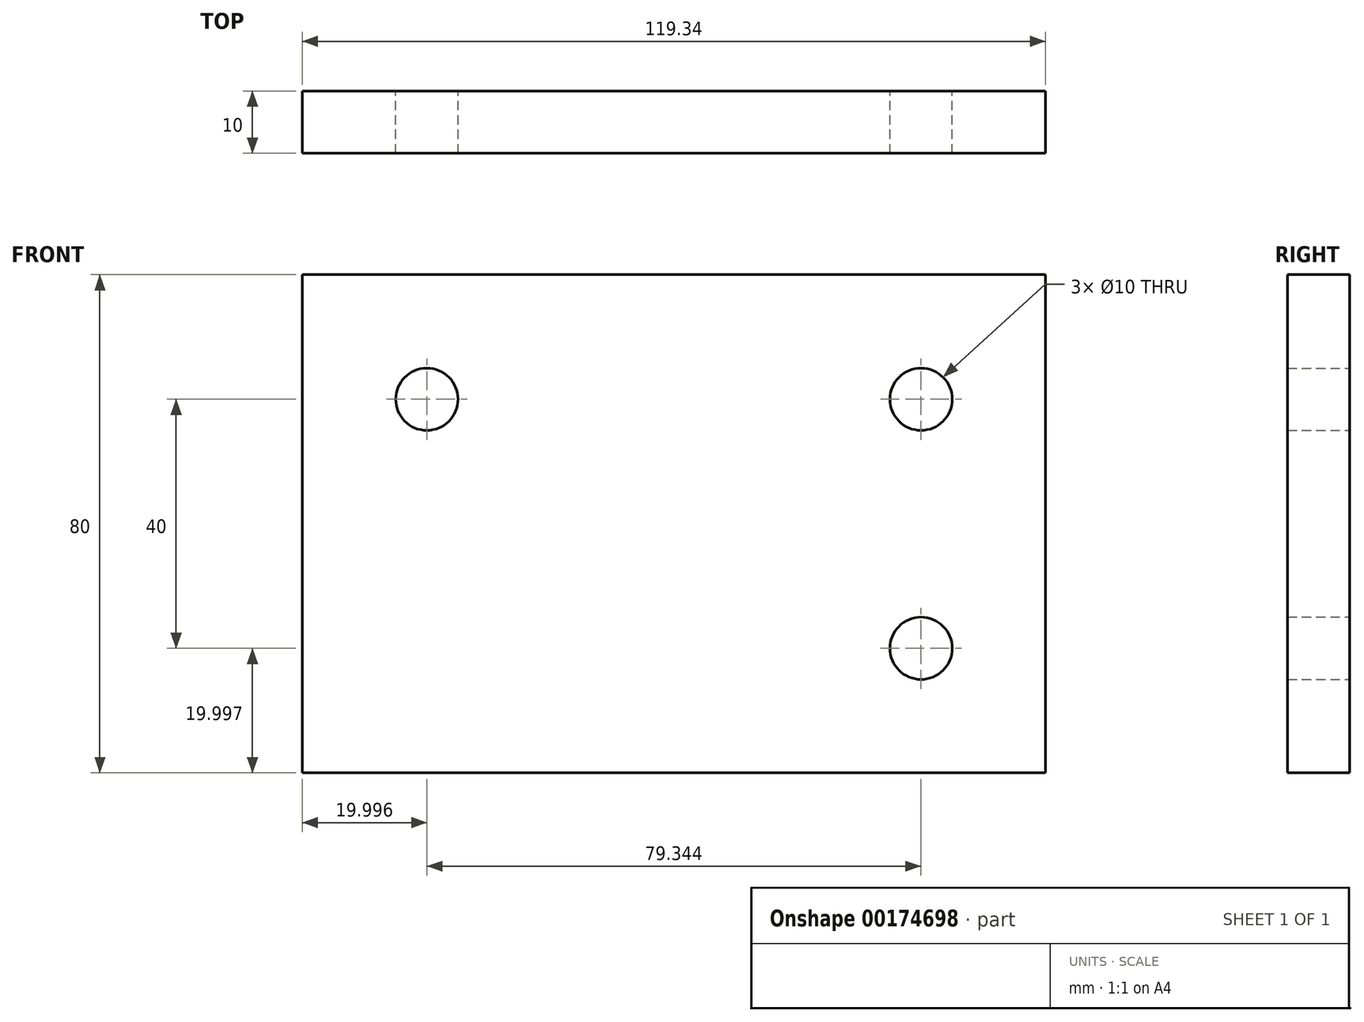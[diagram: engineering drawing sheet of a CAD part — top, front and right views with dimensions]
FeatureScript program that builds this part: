
annotation { "Feature Type Name" : "Feature", "Feature Type Description" : "" }
export const myFeature = defineFeature(function(context is Context, id is Id, definition is map)
    precondition{}
    {
        {
            var Q0;
            Q0=qCreatedBy(makeId("Front.planeOp"),FACE);
            var sketch = newSketch(context, id + "F0", { "sketchPlane" : qUnion([Q0])});
            skLineSegment(sketch, "E0.bottom", {"start": v(-73.45, 55.36) * mm, "end": v(45.89, 55.36) * mm});
            skLineSegment(sketch, "E0.top", {"start": v(-73.45, -24.64) * mm, "end": v(45.89, -24.64) * mm});
            skLineSegment(sketch, "E0.left", {"start": v(-73.45, 55.36) * mm, "end": v(-73.45, -24.64) * mm});
            skLineSegment(sketch, "E0.right", {"start": v(45.89, 55.36) * mm, "end": v(45.89, -24.64) * mm});
            skLineSegment(sketch, "E1", {"start": v(-73.45, 55.36) * mm, "end": v(-73.45, 5.36) * mm});
            skLineSegment(sketch, "E2", {"start": v(-73.45, 5.36) * mm, "end": v(-73.45, -4.64) * mm});
            skLineSegment(sketch, "E3", {"start": v(45.89, 55.36) * mm, "end": v(45.89, 5.36) * mm});
            skLineSegment(sketch, "E4", {"start": v(45.89, 5.36) * mm, "end": v(45.89, -4.64) * mm});
            skLineSegment(sketch, "E5", {"start": v(-73.45, 5.36) * mm, "end": v(45.89, 5.36) * mm});
            skLineSegment(sketch, "E6", {"start": v(-73.45, -4.64) * mm, "end": v(45.89, -4.64) * mm});
            skLineSegment(sketch, "E7", {"start": v(-73.45, 55.36) * mm, "end": v(-73.45, 35.36) * mm});
            skLineSegment(sketch, "E8", {"start": v(-73.45, 35.36) * mm, "end": v(-53.45, 35.36) * mm});
            skLineSegment(sketch, "E9", {"start": v(45.89, 55.36) * mm, "end": v(45.89, 35.36) * mm});
            skLineSegment(sketch, "E10", {"start": v(45.89, 35.36) * mm, "end": v(25.89, 35.36) * mm});
            skCircle(sketch, "E11", {"center": v(-53.45, 35.36) * mm, "radius": 5 * mm});
            skCircle(sketch, "E12", {"center": v(25.89, 35.36) * mm, "radius": 5 * mm});
            skLineSegment(sketch, "E13", {"start": v(25.47, -24.64) * mm, "end": v(45.89, -24.64) * mm});
            skLineSegment(sketch, "E14", {"start": v(45.89, -4.64) * mm, "end": v(45.89, -24.64) * mm});
            skLineSegment(sketch, "E15", {"start": v(45.89, -24.64) * mm, "end": v(45.89, -4.64) * mm});
            skLineSegment(sketch, "E16", {"start": v(45.89, -4.64) * mm, "end": v(25.89, -4.64) * mm});
            skCircle(sketch, "E17", {"center": v(25.89, -4.64) * mm, "radius": 5 * mm});
            skSolve(sketch);
        }
        {
            var Q0;
            Q0 = qSketchRegion(id + "F0", true);
            extrude(context, id + "F1", {"entities" : qUnion([Q0]), "depth" : 10 * mm});
        }
        {
            var Q0;
            Q0=sQuery(id+"F0.wireOp",EDGE,"E5");
            var Q1;
            Q1=sQuery(id+"F0.wireOp",EDGE,"E2");
            var Q2;
            Q2=sQuery(id+"F0.wireOp",EDGE,"E6");
            var Q3;
            Q3=sQuery(id+"F0.wireOp",EDGE,"E4");
            extrude(context, id + "F2", {"bodyType" : ToolBodyType.SURFACE, "surfaceEntities" : qUnion([Q0, Q1, Q2, Q3]), "depth" : 45 * mm});
        }
    });
